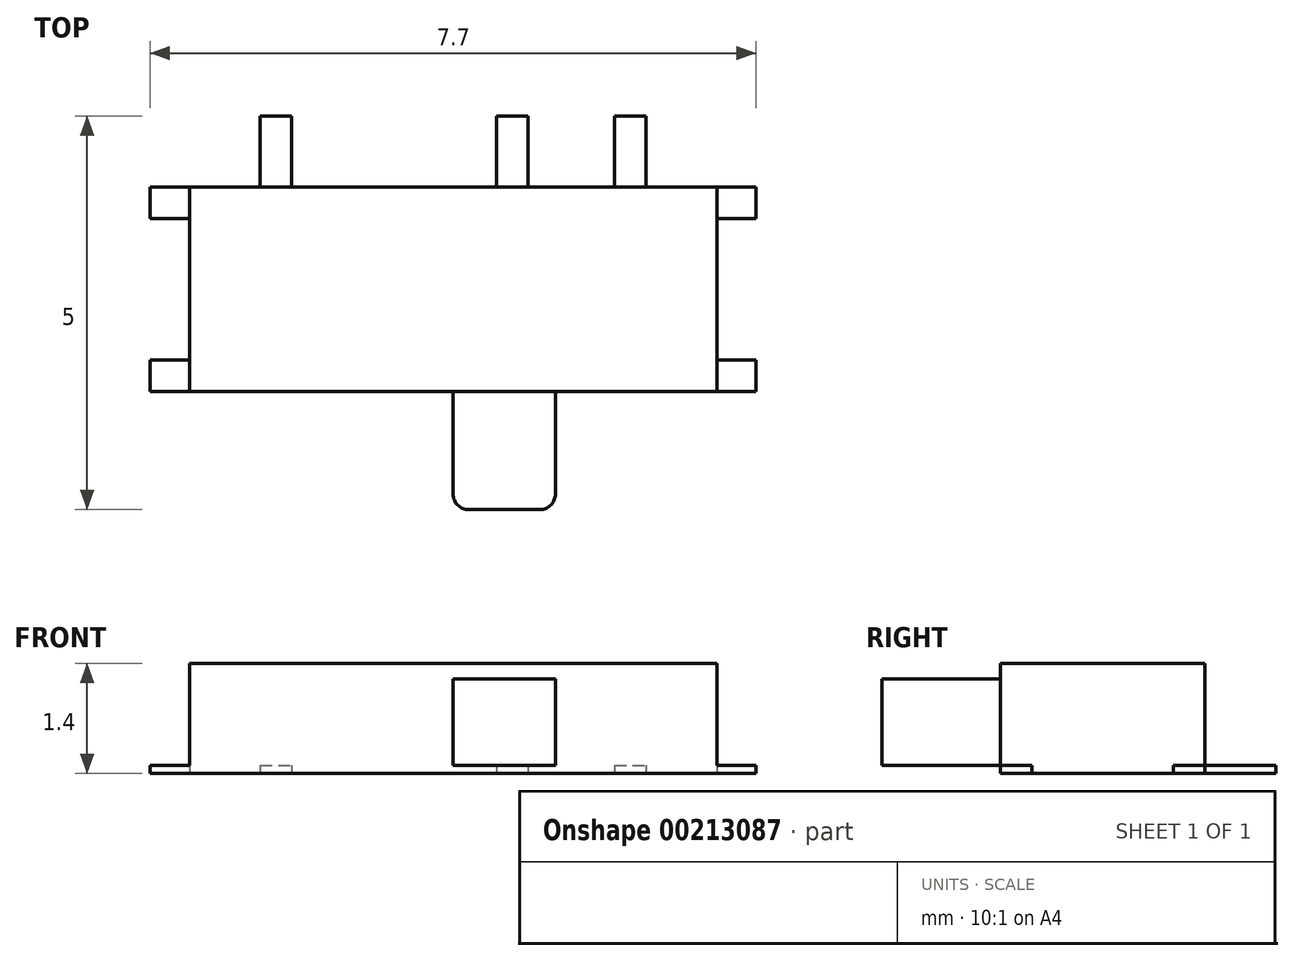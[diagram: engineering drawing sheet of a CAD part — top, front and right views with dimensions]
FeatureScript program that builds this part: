
annotation { "Feature Type Name" : "Feature", "Feature Type Description" : "" }
export const myFeature = defineFeature(function(context is Context, id is Id, definition is map)
    precondition{}
    {
        {
            var Q0;
            Q0=qCreatedBy(makeId("Top.planeOp"),FACE);
            var sketch = newSketch(context, id + "F0", { "sketchPlane" : qUnion([Q0])});
            skLineSegment(sketch, "E0.bottom", {"start": v(-3.35, 1.3) * mm, "end": v(3.35, 1.3) * mm});
            skLineSegment(sketch, "E0.top", {"start": v(-3.35, -1.3) * mm, "end": v(3.35, -1.3) * mm});
            skLineSegment(sketch, "E0.left", {"start": v(-3.35, 1.3) * mm, "end": v(-3.35, -1.3) * mm});
            skLineSegment(sketch, "E0.right", {"start": v(3.35, 1.3) * mm, "end": v(3.35, -1.3) * mm});
            skSolve(sketch);
        }
        {
            var Q0;
            Q0 = qSketchRegion(id + "F0", true);
            extrude(context, id + "F1", {"entities" : qUnion([Q0]), "depth" : 1.4 * mm});
        }
        {
            var Q0;
            Q0=makeQuery(id+"F1.opExtrude","SWEPT_FACE",FACE,{"disambiguationData":[OSD([sQuery(id+"F0.wireOp",EDGE,"E0.top")])]});
            var sketch = newSketch(context, id + "F2", { "sketchPlane" : qUnion([Q0])});
            skLineSegment(sketch, "E1.bottom", {"start": v(0, 1.2) * mm, "end": v(1.3, 1.2) * mm});
            skLineSegment(sketch, "E1.top", {"start": v(0, 0.1) * mm, "end": v(1.3, 0.1) * mm});
            skLineSegment(sketch, "E1.left", {"start": v(0, 1.2) * mm, "end": v(0, 0.1) * mm});
            skLineSegment(sketch, "E1.right", {"start": v(1.3, 1.2) * mm, "end": v(1.3, 0.1) * mm});
            skSolve(sketch);
        }
        {
            var Q0;
            Q0 = qSketchRegion(id + "F2", true);
            extrude(context, id + "F3", {"entities" : qUnion([Q0]), "depth" : 1.5 * mm});
        }
        {
            var Q0;
            Q0=makeQuery(id+"F1.opExtrude","CAP_FACE",FACE,{"disambiguationData":[OSD([sQuery(id+"F0.wireOp",EDGE,"E0.bottom"),sQuery(id+"F0.wireOp",EDGE,"E0.top"),sQuery(id+"F0.wireOp",EDGE,"E0.left"),sQuery(id+"F0.wireOp",EDGE,"E0.right")])],"isStart":true});
            var sketch = newSketch(context, id + "F4", { "sketchPlane" : qUnion([Q0])});
            skLineSegment(sketch, "E2.bottom", {"start": v(-3.35, 1.3) * mm, "end": v(-3.85, 1.3) * mm});
            skLineSegment(sketch, "E2.top", {"start": v(-3.35, 0.9) * mm, "end": v(-3.85, 0.9) * mm});
            skLineSegment(sketch, "E2.left", {"start": v(-3.35, 1.3) * mm, "end": v(-3.35, 0.9) * mm});
            skLineSegment(sketch, "E2.right", {"start": v(-3.85, 1.3) * mm, "end": v(-3.85, 0.9) * mm});
            skLineSegment(sketch, "E3.MirrorCS", {"start": v(-3.85, -1.3) * mm, "end": v(-3.85, -0.9) * mm});
            skLineSegment(sketch, "E4.MirrorCS", {"start": v(-3.35, -1.3) * mm, "end": v(-3.35, -0.9) * mm});
            skLineSegment(sketch, "E5.MirrorCS", {"start": v(-3.35, -1.3) * mm, "end": v(-3.85, -1.3) * mm});
            skLineSegment(sketch, "E6.MirrorCS", {"start": v(-3.35, -0.9) * mm, "end": v(-3.85, -0.9) * mm});
            skLineSegment(sketch, "E7.MirrorCS", {"start": v(3.35, -0.9) * mm, "end": v(3.85, -0.9) * mm});
            skLineSegment(sketch, "E8.MirrorCS", {"start": v(3.35, -1.3) * mm, "end": v(3.85, -1.3) * mm});
            skLineSegment(sketch, "E9.MirrorCS", {"start": v(3.35, -1.3) * mm, "end": v(3.35, -0.9) * mm});
            skLineSegment(sketch, "E10.MirrorCS", {"start": v(3.35, 1.3) * mm, "end": v(3.85, 1.3) * mm});
            skLineSegment(sketch, "E11.MirrorCS", {"start": v(3.35, 0.9) * mm, "end": v(3.85, 0.9) * mm});
            skLineSegment(sketch, "E12.MirrorCS", {"start": v(3.35, 1.3) * mm, "end": v(3.35, 0.9) * mm});
            skLineSegment(sketch, "E13.MirrorCS", {"start": v(3.85, -1.3) * mm, "end": v(3.85, -0.9) * mm});
            skLineSegment(sketch, "E14.MirrorCS", {"start": v(3.85, 1.3) * mm, "end": v(3.85, 0.9) * mm});
            skLineSegment(sketch, "E15.bottom", {"start": v(0.55, -1.3) * mm, "end": v(0.95, -1.3) * mm});
            skLineSegment(sketch, "E15.top", {"start": v(0.55, -2.2) * mm, "end": v(0.95, -2.2) * mm});
            skLineSegment(sketch, "E15.left", {"start": v(0.55, -1.3) * mm, "end": v(0.55, -2.2) * mm});
            skLineSegment(sketch, "E15.right", {"start": v(0.95, -1.3) * mm, "end": v(0.95, -2.2) * mm});
            skLineSegment(sketch, "E16.bottom", {"start": v(2.05, -1.3) * mm, "end": v(2.45, -1.3) * mm});
            skLineSegment(sketch, "E16.top", {"start": v(2.05, -2.2) * mm, "end": v(2.45, -2.2) * mm});
            skLineSegment(sketch, "E16.left", {"start": v(2.05, -1.3) * mm, "end": v(2.05, -2.2) * mm});
            skLineSegment(sketch, "E16.right", {"start": v(2.45, -1.3) * mm, "end": v(2.45, -2.2) * mm});
            skLineSegment(sketch, "E17.bottom", {"start": v(-2.45, -1.3) * mm, "end": v(-2.05, -1.3) * mm});
            skLineSegment(sketch, "E17.top", {"start": v(-2.45, -2.2) * mm, "end": v(-2.05, -2.2) * mm});
            skLineSegment(sketch, "E17.left", {"start": v(-2.45, -1.3) * mm, "end": v(-2.45, -2.2) * mm});
            skLineSegment(sketch, "E17.right", {"start": v(-2.05, -1.3) * mm, "end": v(-2.05, -2.2) * mm});
            skSolve(sketch);
        }
        {
            var Q0;
            Q0 = qSketchRegion(id + "F4", true);
            extrude(context, id + "F5", {"entities" : qUnion([Q0]), "operationType" : NewBodyOperationType.ADD, "oppositeDirection" : true, "depth" : .1 * mm});
        }
        {
            var Q0;
            Q0=makeQuery(id+"F3.opExtrude","CAP_EDGE",EDGE,{"disambiguationData":[OSD([sQuery(id+"F2.wireOp",EDGE,"E1.left")])],"isStart":false});
            var Q1;
            Q1=makeQuery(id+"F3.opExtrude","CAP_EDGE",EDGE,{"disambiguationData":[OSD([sQuery(id+"F2.wireOp",EDGE,"E1.right")])],"isStart":false});
            fillet(context, id + "F6", {"entities" : qUnion([Q0, Q1]), "radius" : .2 * mm, "tangentPropagation" : true, "allowEdgeOverflow" : false});
        }
    });
